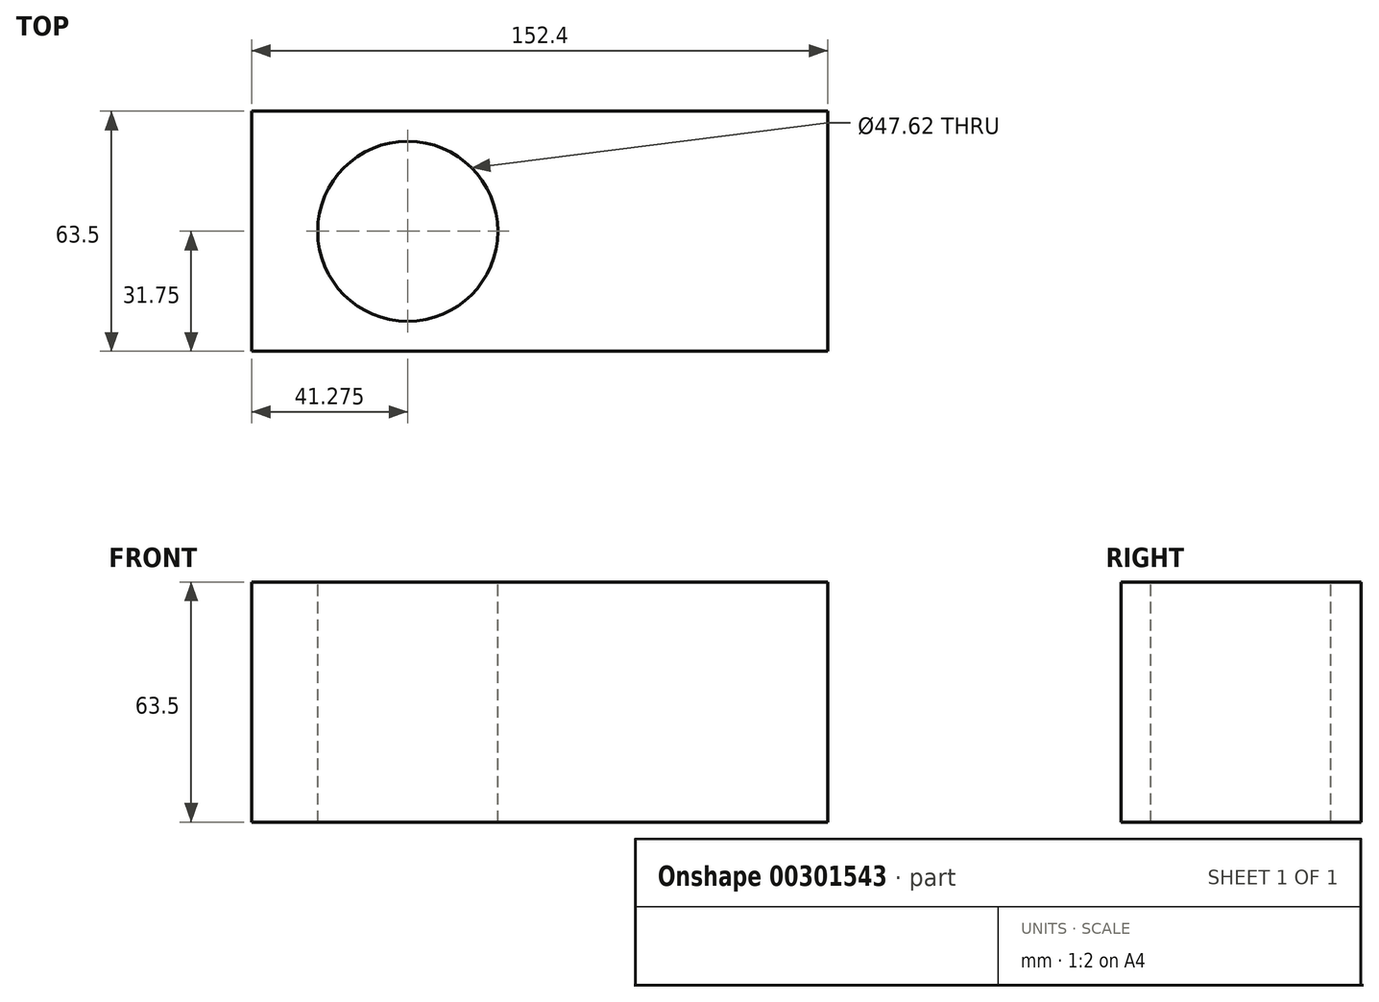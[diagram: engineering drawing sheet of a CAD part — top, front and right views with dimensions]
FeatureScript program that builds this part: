
annotation { "Feature Type Name" : "Feature", "Feature Type Description" : "" }
export const myFeature = defineFeature(function(context is Context, id is Id, definition is map)
    precondition{}
    {
        {
            var Q0;
            Q0=qCreatedBy(makeId("Front.planeOp"),FACE);
            var sketch = newSketch(context, id + "F0", { "sketchPlane" : qUnion([Q0])});
            skLineSegment(sketch, "E0.bottom", {"start": v(-76.2, 31.75) * mm, "end": v(76.2, 31.75) * mm});
            skLineSegment(sketch, "E0.top", {"start": v(-76.2, -31.75) * mm, "end": v(76.2, -31.75) * mm});
            skLineSegment(sketch, "E0.left", {"start": v(-76.2, 31.75) * mm, "end": v(-76.2, -31.75) * mm});
            skLineSegment(sketch, "E0.right", {"start": v(76.2, 31.75) * mm, "end": v(76.2, -31.75) * mm});
            skSolve(sketch);
        }
        {
            var Q0;
            Q0=makeQuery(id+"F0.imprint","IMPRINT",FACE,{"disambiguationData":[TD([[makeQuery(id+"F0.imprint","IMPRINT",EDGE,{"derivedFrom":sQuery(id+"F0.wireOp",EDGE,"E0.bottom")}),-1.0]])]});
            extrude(context, id + "F1", {"entities" : qUnion([Q0]), "endBound" : BoundingType.SYMMETRIC, "depth" : 63.5 * mm});
        }
        {
            var Q0;
            Q0=makeQuery(id+"F1.opExtrude","SWEPT_FACE",FACE,{"disambiguationData":[OSD([sQuery(id+"F0.wireOp",EDGE,"E0.bottom")])]});
            var sketch = newSketch(context, id + "F2", { "sketchPlane" : qUnion([Q0])});
            skPoint(sketch, "E1", {"position": v(-34.92, 0) * mm});
            skSolve(sketch);
        }
        {
            var Q0;
            Q0=sQuery(id+"F2.wireOp",VERTEX,"E1");
            var Q1;
            Q1=makeQuery(id+"F1.opExtrude","SWEPT_BODY",BODY,{"disambiguationData":[OSD([sQuery(id+"F0.wireOp",EDGE,"E0.bottom"),sQuery(id+"F0.wireOp",EDGE,"E0.top"),sQuery(id+"F0.wireOp",EDGE,"E0.left"),sQuery(id+"F0.wireOp",EDGE,"E0.right")])]});
            hole(context, id + "F3", {"style" : HoleStyle.SIMPLE, "endStyle" : HoleEndStyle.THROUGH, "holeDiameter" : 47.62 * mm, "tappedDepth" : 12.7 * mm, "tapClearance" : 3, "locations" : qUnion([Q0]), "scope" : qUnion([Q1])});
        }
    });
